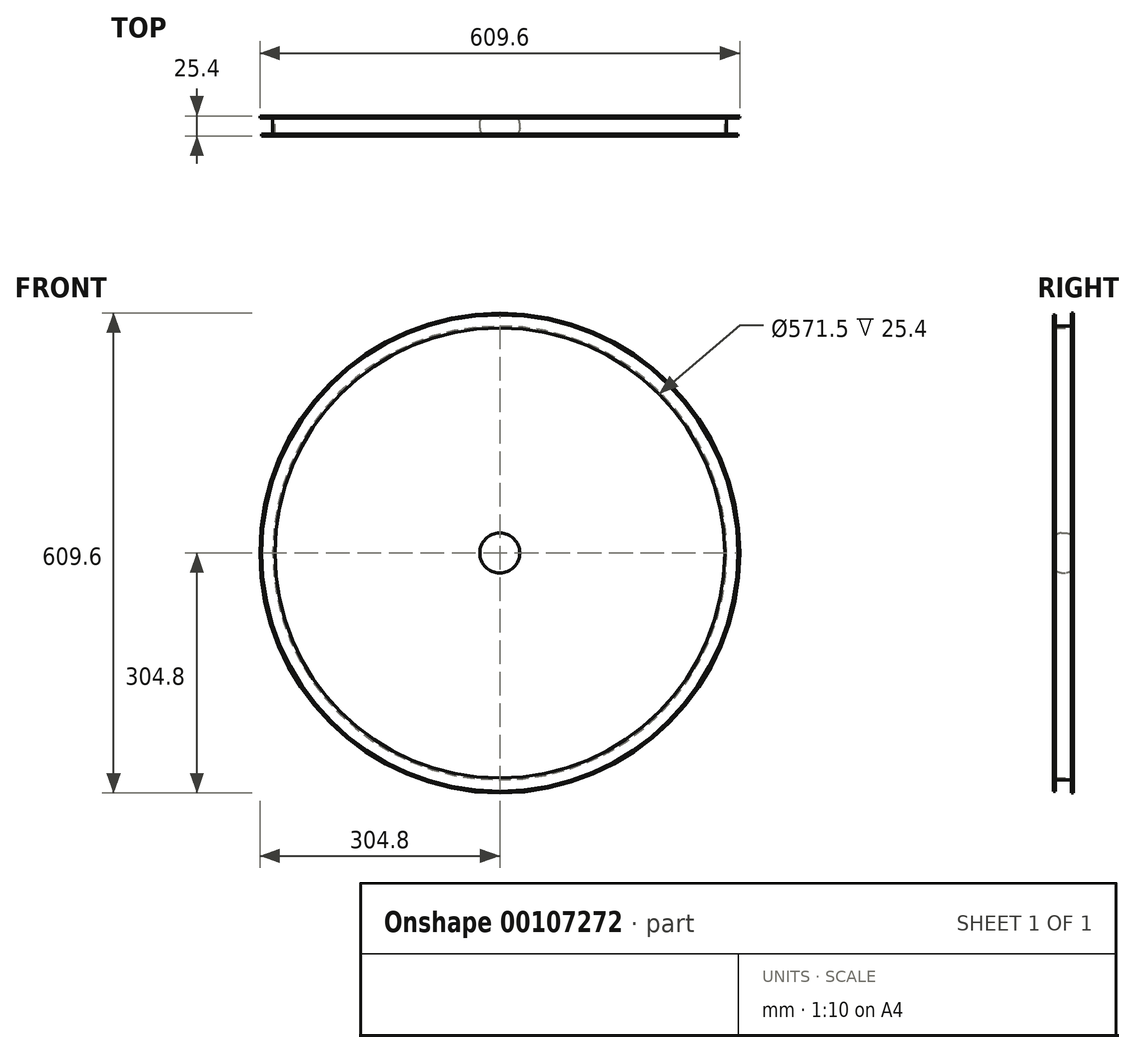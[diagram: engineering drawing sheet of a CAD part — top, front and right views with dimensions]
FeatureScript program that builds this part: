
annotation { "Feature Type Name" : "Feature", "Feature Type Description" : "" }
export const myFeature = defineFeature(function(context is Context, id is Id, definition is map)
    precondition{}
    {
        {
            var Q0;
            Q0=qCreatedBy(makeId("Front.planeOp"),FACE);
            var sketch = newSketch(context, id + "F0", { "sketchPlane" : qUnion([Q0])});
            skCircle(sketch, "E0", {"center": v(0, 0) * mm, "radius": 304.8 * mm});
            skSolve(sketch);
        }
        {
            var Q0;
            Q0=makeQuery(id+"F0.imprint","IMPRINT",FACE,{"disambiguationData":[TD([[makeQuery(id+"F0.imprint","IMPRINT",EDGE,{"derivedFrom":sQuery(id+"F0.wireOp",EDGE,"E0")}),1.0]])]});
            var sketch = newSketch(context, id + "F1", { "sketchPlane" : qUnion([Q0])});
            skCircle(sketch, "E1", {"center": v(0, 0) * mm, "radius": 279.4 * mm, "construction": true});
            skSolve(sketch);
        }
        {
            var Q0;
            Q0=makeQuery(id+"F0.imprint","IMPRINT",FACE,{"disambiguationData":[TD([[makeQuery(id+"F0.imprint","IMPRINT",EDGE,{"derivedFrom":sQuery(id+"F0.wireOp",EDGE,"E0")}),1.0]])]});
            extrude(context, id + "F2", {"entities" : qUnion([Q0]), "depth" : 25.4 * mm, "hasDraft" : true, "draftAngle" : 5 * degree, "draftPullDirection" : true});
        }
        {
            var Q0;
            Q0=sQuery(id+"F1.wireOp",VERTEX,"E1.center");
            var Q1;
            Q1=makeQuery(id+"F2.opExtrude","SWEPT_BODY",BODY,{"disambiguationData":[OSD([sQuery(id+"F0.wireOp",EDGE,"E0")])]});
            hole(context, id + "F3", {"style" : HoleStyle.SIMPLE, "endStyle" : HoleEndStyle.THROUGH, "oppositeDirection" : true, "holeDiameter" : 571.5 * mm, "locations" : qUnion([Q0]), "scope" : qUnion([Q1]), "isTappedThrough" : true});
        }
        {
            var Q0;
            Q0=makeQuery(id+"F2.opExtrude","SWEPT_FACE",FACE,{"disambiguationData":[OSD([sQuery(id+"F0.wireOp",EDGE,"E0")])]});
            shell(context, id + "F4", {"entities" : qUnion([Q0]), "thickness" : 2.54 * mm});
        }
        {
            var Q0;
            Q0=makeQuery(id+"F1.imprint","IMPRINT",FACE,{"disambiguationData":[TD([[makeQuery(id+"F1.imprint","IMPRINT",EDGE,{"derivedFrom":makeQuery(id+"F0.imprint","IMPRINT",EDGE,{"derivedFrom":sQuery(id+"F0.wireOp",EDGE,"E0")})}),1.0]])]});
            var sketch = newSketch(context, id + "F5", { "sketchPlane" : qUnion([Q0])});
            skCircle(sketch, "E2", {"center": v(0, 0) * mm, "radius": 25.4 * mm});
            skSolve(sketch);
        }
        {
            var Q0;
            Q0=makeQuery(id+"F5.imprint","IMPRINT",FACE,{"disambiguationData":[TD([[makeQuery(id+"F5.imprint","IMPRINT",EDGE,{"derivedFrom":sQuery(id+"F5.wireOp",EDGE,"E2")}),1.0]])]});
            extrude(context, id + "F6", {"entities" : qUnion([Q0]), "depth" : 25.4 * mm});
        }
        {
            var Q0;
            Q0=makeQuery(id+"F6.opExtrude","CAP_EDGE",EDGE,{"disambiguationData":[OSD([sQuery(id+"F5.wireOp",EDGE,"E2")])],"isStart":false});
            fillet(context, id + "F7", {"entities" : qUnion([Q0]), "radius" : 10.16 * mm, "tangentPropagation" : true, "allowEdgeOverflow" : false});
        }
        {
            var Q0;
            Q0=makeQuery(id+"F6.opExtrude","CAP_EDGE",EDGE,{"disambiguationData":[OSD([sQuery(id+"F5.wireOp",EDGE,"E2")])],"isStart":true});
            fillet(context, id + "F8", {"entities" : qUnion([Q0]), "radius" : 10.16 * mm, "tangentPropagation" : true, "allowEdgeOverflow" : false});
        }
    });
